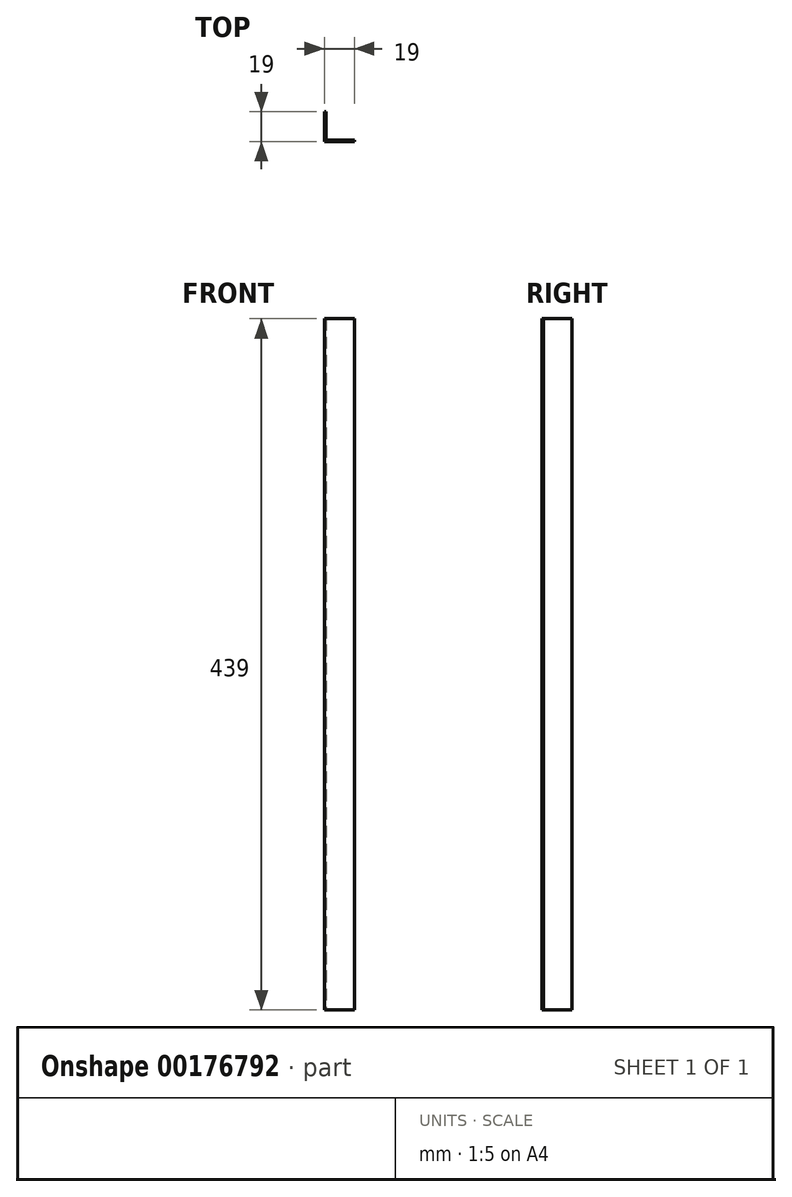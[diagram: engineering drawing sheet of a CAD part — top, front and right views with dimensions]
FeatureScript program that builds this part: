
annotation { "Feature Type Name" : "Feature", "Feature Type Description" : "" }
export const myFeature = defineFeature(function(context is Context, id is Id, definition is map)
    precondition{}
    {
        {
            var Q0;
            Q0=qCreatedBy(makeId("Top.planeOp"),FACE);
            var sketch = newSketch(context, id + "F0", { "sketchPlane" : qUnion([Q0])});
            skLineSegment(sketch, "E0", {"start": v(0, 0) * mm, "end": v(19, 0) * mm});
            skLineSegment(sketch, "E1", {"start": v(0, 0) * mm, "end": v(0, 19) * mm});
            skLineSegment(sketch, "E2", {"start": v(0, 19) * mm, "end": v(1, 19) * mm});
            skLineSegment(sketch, "E3", {"start": v(1, 19) * mm, "end": v(1, 1) * mm});
            skLineSegment(sketch, "E4", {"start": v(1, 1) * mm, "end": v(19, 1) * mm});
            skLineSegment(sketch, "E5", {"start": v(19, 1) * mm, "end": v(19, 0) * mm});
            skSolve(sketch);
        }
        {
            var Q0;
            Q0=makeQuery(id+"F0.imprint","IMPRINT",FACE,{"disambiguationData":[TD([[makeQuery(id+"F0.imprint","IMPRINT",EDGE,{"derivedFrom":sQuery(id+"F0.wireOp",EDGE,"E0")}),1.0]])]});
            extrude(context, id + "F1", {"entities" : qUnion([Q0]), "depth" : 439 * mm});
        }
    });
